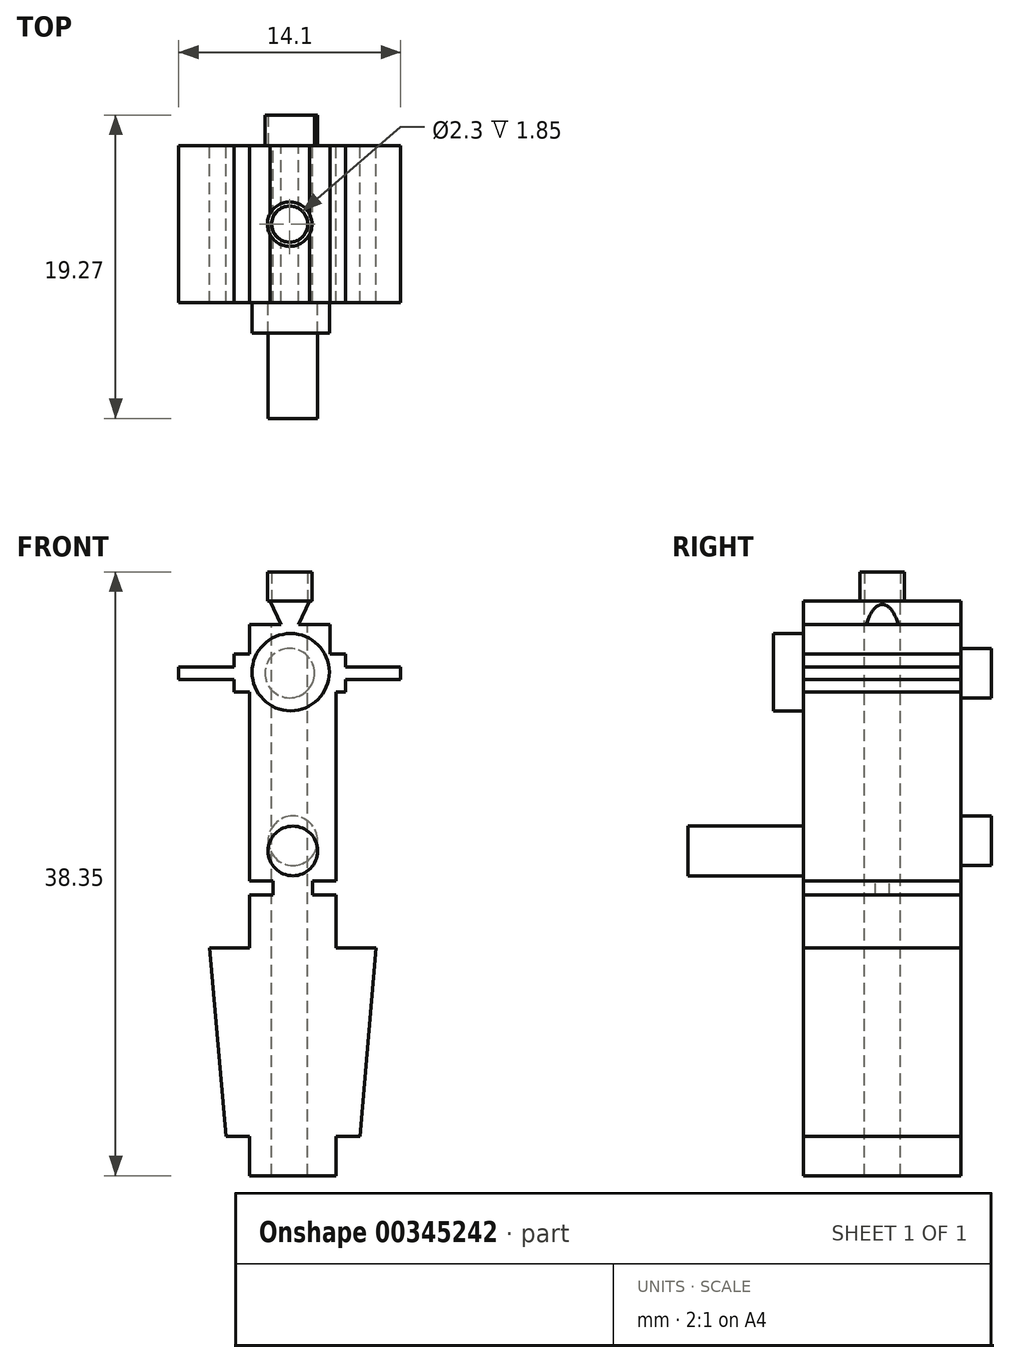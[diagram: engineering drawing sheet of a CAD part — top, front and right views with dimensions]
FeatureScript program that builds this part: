
annotation { "Feature Type Name" : "Feature", "Feature Type Description" : "" }
export const myFeature = defineFeature(function(context is Context, id is Id, definition is map)
    precondition{}
    {
        {
            var Q0;
            Q0=qCreatedBy(makeId("Front.planeOp"),FACE);
            var sketch = newSketch(context, id + "F0", { "sketchPlane" : qUnion([Q0])});
            skLineSegment(sketch, "E0", {"start": v(0, 0) * mm, "end": v(5.5, 0) * mm});
            skLineSegment(sketch, "E1", {"start": v(5.5, 0) * mm, "end": v(5.5, 2.5) * mm});
            skLineSegment(sketch, "E2", {"start": v(0, 0) * mm, "end": v(0, 2.5) * mm});
            skLineSegment(sketch, "E3", {"start": v(0, 2.5) * mm, "end": v(-1.5, 2.5) * mm});
            skLineSegment(sketch, "E4", {"start": v(5.5, 2.5) * mm, "end": v(7, 2.5) * mm});
            skLineSegment(sketch, "E5", {"start": v(7, 2.5) * mm, "end": v(8.05, 14.45) * mm});
            skLineSegment(sketch, "E6", {"start": v(-1.5, 2.5) * mm, "end": v(-2.55, 14.45) * mm});
            skLineSegment(sketch, "E7", {"start": v(8.05, 14.45) * mm, "end": v(5.5, 14.45) * mm});
            skLineSegment(sketch, "E8", {"start": v(-2.55, 14.45) * mm, "end": v(0, 14.45) * mm});
            skLineSegment(sketch, "E9", {"start": v(0, 14.45) * mm, "end": v(0, 17.82) * mm});
            skLineSegment(sketch, "E10", {"start": v(5.5, 14.45) * mm, "end": v(5.5, 17.82) * mm});
            skLineSegment(sketch, "E11", {"start": v(5.5, 17.82) * mm, "end": v(4, 17.82) * mm});
            skLineSegment(sketch, "E12", {"start": v(0, 17.82) * mm, "end": v(1.5, 17.82) * mm});
            skLineSegment(sketch, "E13", {"start": v(4, 17.82) * mm, "end": v(4, 18.72) * mm});
            skLineSegment(sketch, "E14", {"start": v(1.5, 17.82) * mm, "end": v(1.5, 18.72) * mm});
            skLineSegment(sketch, "E15", {"start": v(1.5, 18.72) * mm, "end": v(0, 18.72) * mm});
            skLineSegment(sketch, "E16", {"start": v(4, 18.72) * mm, "end": v(5.5, 18.72) * mm});
            skLineSegment(sketch, "E17", {"start": v(5.5, 18.72) * mm, "end": v(5.5, 30.72) * mm});
            skLineSegment(sketch, "E18", {"start": v(0, 18.72) * mm, "end": v(0, 30.72) * mm});
            skLineSegment(sketch, "E19", {"start": v(5.1, 33.12) * mm, "end": v(6.1, 33.12) * mm});
            skLineSegment(sketch, "E20", {"start": v(6.1, 33.12) * mm, "end": v(6.1, 32.32) * mm});
            skLineSegment(sketch, "E21", {"start": v(6.1, 32.32) * mm, "end": v(9.6, 32.32) * mm});
            skLineSegment(sketch, "E22", {"start": v(9.6, 32.32) * mm, "end": v(9.6, 31.52) * mm});
            skLineSegment(sketch, "E23", {"start": v(9.6, 31.52) * mm, "end": v(6.1, 31.52) * mm});
            skLineSegment(sketch, "E24", {"start": v(6.1, 31.52) * mm, "end": v(6.1, 30.72) * mm});
            skLineSegment(sketch, "E25", {"start": v(6.1, 30.72) * mm, "end": v(5.5, 30.72) * mm});
            skLineSegment(sketch, "E26", {"start": v(0, 30.72) * mm, "end": v(-1, 30.72) * mm});
            skLineSegment(sketch, "E27", {"start": v(-1, 30.72) * mm, "end": v(-1, 31.52) * mm});
            skLineSegment(sketch, "E28", {"start": v(-1, 31.52) * mm, "end": v(-4.5, 31.52) * mm});
            skLineSegment(sketch, "E29", {"start": v(-4.5, 31.52) * mm, "end": v(-4.5, 32.32) * mm});
            skLineSegment(sketch, "E30", {"start": v(-4.5, 32.32) * mm, "end": v(-1, 32.32) * mm});
            skLineSegment(sketch, "E31", {"start": v(-1, 32.32) * mm, "end": v(-1, 33.12) * mm});
            skLineSegment(sketch, "E32", {"start": v(-1, 33.12) * mm, "end": v(0, 33.12) * mm});
            skLineSegment(sketch, "E33", {"start": v(0, 33.12) * mm, "end": v(0, 35) * mm});
            skLineSegment(sketch, "E34", {"start": v(0, 35) * mm, "end": v(2, 35) * mm});
            skLineSegment(sketch, "E35", {"start": v(2, 35) * mm, "end": v(1.3, 36.5) * mm});
            skLineSegment(sketch, "E36", {"start": v(1.3, 36.5) * mm, "end": v(3.8, 36.5) * mm});
            skLineSegment(sketch, "E37", {"start": v(3.8, 36.5) * mm, "end": v(3.1, 35) * mm});
            skLineSegment(sketch, "E38", {"start": v(3.1, 35) * mm, "end": v(5.1, 35) * mm});
            skLineSegment(sketch, "E39", {"start": v(5.1, 35) * mm, "end": v(5.1, 33.12) * mm});
            skSolve(sketch);
        }
        {
            var Q0;
            Q0 = qSketchRegion(id + "F0", true);
            extrude(context, id + "F1", {"entities" : qUnion([Q0]), "depth" : 10 * mm});
        }
        {
            var Q0;
            Q0=makeQuery(id+"F1.opExtrude","CAP_FACE",FACE,{"disambiguationData":[OSD([sQuery(id+"F0.wireOp",EDGE,"E0"),sQuery(id+"F0.wireOp",EDGE,"E1"),sQuery(id+"F0.wireOp",EDGE,"E2"),sQuery(id+"F0.wireOp",EDGE,"E3"),sQuery(id+"F0.wireOp",EDGE,"E4"),sQuery(id+"F0.wireOp",EDGE,"E5"),sQuery(id+"F0.wireOp",EDGE,"E6"),sQuery(id+"F0.wireOp",EDGE,"E7"),sQuery(id+"F0.wireOp",EDGE,"E8"),sQuery(id+"F0.wireOp",EDGE,"E9"),sQuery(id+"F0.wireOp",EDGE,"E10"),sQuery(id+"F0.wireOp",EDGE,"E11"),sQuery(id+"F0.wireOp",EDGE,"E12"),sQuery(id+"F0.wireOp",EDGE,"E13"),sQuery(id+"F0.wireOp",EDGE,"E14"),sQuery(id+"F0.wireOp",EDGE,"E15"),sQuery(id+"F0.wireOp",EDGE,"E16"),sQuery(id+"F0.wireOp",EDGE,"E17"),sQuery(id+"F0.wireOp",EDGE,"E18"),sQuery(id+"F0.wireOp",EDGE,"E19"),sQuery(id+"F0.wireOp",EDGE,"E20"),sQuery(id+"F0.wireOp",EDGE,"E21"),sQuery(id+"F0.wireOp",EDGE,"E22"),sQuery(id+"F0.wireOp",EDGE,"E23"),sQuery(id+"F0.wireOp",EDGE,"E24"),sQuery(id+"F0.wireOp",EDGE,"E25"),sQuery(id+"F0.wireOp",EDGE,"E26"),sQuery(id+"F0.wireOp",EDGE,"E27"),sQuery(id+"F0.wireOp",EDGE,"E28"),sQuery(id+"F0.wireOp",EDGE,"E29"),sQuery(id+"F0.wireOp",EDGE,"E30"),sQuery(id+"F0.wireOp",EDGE,"E31"),sQuery(id+"F0.wireOp",EDGE,"E32"),sQuery(id+"F0.wireOp",EDGE,"E33"),sQuery(id+"F0.wireOp",EDGE,"E34"),sQuery(id+"F0.wireOp",EDGE,"E35"),sQuery(id+"F0.wireOp",EDGE,"E36"),sQuery(id+"F0.wireOp",EDGE,"E37"),sQuery(id+"F0.wireOp",EDGE,"E38"),sQuery(id+"F0.wireOp",EDGE,"E39")])],"isStart":false});
            var sketch = newSketch(context, id + "F2", { "sketchPlane" : qUnion([Q0])});
            skCircle(sketch, "E40", {"center": v(2.6, 31.98) * mm, "radius": 2.45 * mm});
            skCircle(sketch, "E41", {"center": v(2.75, 20.63) * mm, "radius": 1.57 * mm});
            skPoint(sketch, "E41.centerSnap0", {"position": v(2.75, 0) * mm});
            skSolve(sketch);
        }
        {
            var Q0;
            Q0=makeQuery(id+"F2.imprint","IMPRINT",FACE,{"disambiguationData":[TD([[makeQuery(id+"F2.imprint","IMPRINT",EDGE,{"derivedFrom":sQuery(id+"F2.wireOp",EDGE,"E40")}),1.0]])]});
            var Q1;
            Q1=makeQuery(id+"F2.imprint","IMPRINT",FACE,{"disambiguationData":[TD([[makeQuery(id+"F2.imprint","IMPRINT",EDGE,{"derivedFrom":sQuery(id+"F2.wireOp",EDGE,"E41")}),1.0]])]});
            extrude(context, id + "F3", {"entities" : qUnion([Q0, Q1]), "operationType" : NewBodyOperationType.ADD, "depth" : 1.93 * mm});
        }
        {
            var Q0;
            Q0=makeQuery(id+"F3.opExtrude","CAP_FACE",FACE,{"disambiguationData":[OSD([sQuery(id+"F2.wireOp",EDGE,"E41")])],"isStart":false});
            extrude(context, id + "F4", {"entities" : qUnion([Q0]), "operationType" : NewBodyOperationType.ADD, "depth" : 5.4 * mm});
        }
        {
            var Q0;
            Q0=makeQuery(id+"F1.opExtrude","SWEPT_FACE",FACE,{"disambiguationData":[OSD([sQuery(id+"F0.wireOp",EDGE,"E36")])]});
            var sketch = newSketch(context, id + "F5", { "sketchPlane" : qUnion([Q0])});
            skCircle(sketch, "E42", {"center": v(2.55, -5) * mm, "radius": 1.14 * mm});
            skPoint(sketch, "E42.centerSnap0", {"position": v(2.55, 0) * mm});
            skPoint(sketch, "E42.centerSnap1", {"position": v(1.3, -5) * mm});
            skSolve(sketch);
        }
        {
            var Q0;
            Q0 = qSketchRegion(id + "F5", true);
            extrude(context, id + "F6", {"entities" : qUnion([Q0]), "operationType" : NewBodyOperationType.REMOVE, "oppositeDirection" : true, "depth" : 90 * mm});
        }
        {
            var Q0;
            Q0=makeQuery(id+"F1.opExtrude","SWEPT_FACE",FACE,{"disambiguationData":[OSD([sQuery(id+"F0.wireOp",EDGE,"E36")])]});
            var sketch = newSketch(context, id + "F7", { "sketchPlane" : qUnion([Q0])});
            skCircle(sketch, "E43", {"center": v(2.55, -5) * mm, "radius": 1.42 * mm});
            skSolve(sketch);
        }
        {
            var Q0;
            Q0 = qSketchRegion(id + "F7", true);
            extrude(context, id + "F8", {"entities" : qUnion([Q0]), "operationType" : NewBodyOperationType.ADD, "depth" : 1.85 * mm});
        }
        {
            var Q0;
            Q0=makeQuery(id+"F8.boolean.opBoolean","SPLIT",FACE,{"disambiguationData":[TD([makeQuery(id+"F6.boolean.opBoolean","COPY",FACE,{"derivedFrom":makeQuery(id+"F6.opExtrude","SWEPT_FACE",FACE,{"disambiguationData":[OSD([sQuery(id+"F5.wireOp",EDGE,"E42")])]})})])],"derivedFrom":makeQuery(id+"F8.opExtrude","CAP_FACE",FACE,{"disambiguationData":[OSD([sQuery(id+"F7.wireOp",EDGE,"E43")])],"isStart":true})});
            var sketch = newSketch(context, id + "F9", { "sketchPlane" : qUnion([Q0])});
            skCircle(sketch, "E44", {"center": v(2.55, 5) * mm, "radius": 1.15 * mm});
            skSolve(sketch);
        }
        {
            var Q0;
            Q0 = qSketchRegion(id + "F9", true);
            extrude(context, id + "F10", {"entities" : qUnion([Q0]), "operationType" : NewBodyOperationType.REMOVE, "oppositeDirection" : true, "depth" : 90 * mm});
        }
        {
            var Q0;
            Q0=makeQuery(id+"F1.opExtrude","CAP_FACE",FACE,{"disambiguationData":[OSD([sQuery(id+"F0.wireOp",EDGE,"E0"),sQuery(id+"F0.wireOp",EDGE,"E1"),sQuery(id+"F0.wireOp",EDGE,"E2"),sQuery(id+"F0.wireOp",EDGE,"E3"),sQuery(id+"F0.wireOp",EDGE,"E4"),sQuery(id+"F0.wireOp",EDGE,"E5"),sQuery(id+"F0.wireOp",EDGE,"E6"),sQuery(id+"F0.wireOp",EDGE,"E7"),sQuery(id+"F0.wireOp",EDGE,"E8"),sQuery(id+"F0.wireOp",EDGE,"E9"),sQuery(id+"F0.wireOp",EDGE,"E10"),sQuery(id+"F0.wireOp",EDGE,"E11"),sQuery(id+"F0.wireOp",EDGE,"E12"),sQuery(id+"F0.wireOp",EDGE,"E13"),sQuery(id+"F0.wireOp",EDGE,"E14"),sQuery(id+"F0.wireOp",EDGE,"E15"),sQuery(id+"F0.wireOp",EDGE,"E16"),sQuery(id+"F0.wireOp",EDGE,"E17"),sQuery(id+"F0.wireOp",EDGE,"E18"),sQuery(id+"F0.wireOp",EDGE,"E19"),sQuery(id+"F0.wireOp",EDGE,"E20"),sQuery(id+"F0.wireOp",EDGE,"E21"),sQuery(id+"F0.wireOp",EDGE,"E22"),sQuery(id+"F0.wireOp",EDGE,"E23"),sQuery(id+"F0.wireOp",EDGE,"E24"),sQuery(id+"F0.wireOp",EDGE,"E25"),sQuery(id+"F0.wireOp",EDGE,"E26"),sQuery(id+"F0.wireOp",EDGE,"E27"),sQuery(id+"F0.wireOp",EDGE,"E28"),sQuery(id+"F0.wireOp",EDGE,"E29"),sQuery(id+"F0.wireOp",EDGE,"E30"),sQuery(id+"F0.wireOp",EDGE,"E31"),sQuery(id+"F0.wireOp",EDGE,"E32"),sQuery(id+"F0.wireOp",EDGE,"E33"),sQuery(id+"F0.wireOp",EDGE,"E34"),sQuery(id+"F0.wireOp",EDGE,"E35"),sQuery(id+"F0.wireOp",EDGE,"E36"),sQuery(id+"F0.wireOp",EDGE,"E37"),sQuery(id+"F0.wireOp",EDGE,"E38"),sQuery(id+"F0.wireOp",EDGE,"E39")])],"isStart":true});
            var sketch = newSketch(context, id + "F11", { "sketchPlane" : qUnion([Q0])});
            skPoint(sketch, "E45.centerSnap0", {"position": v(-2.55, 36.5) * mm});
            skPoint(sketch, "E45.centerSnap1", {"position": v(4.5, 31.92) * mm});
            skCircle(sketch, "E46", {"center": v(-2.55, 31.92) * mm, "radius": 1.57 * mm});
            skSolve(sketch);
        }
        {
            var Q0;
            Q0 = qSketchRegion(id + "F11", true);
            extrude(context, id + "F12", {"entities" : qUnion([Q0]), "operationType" : NewBodyOperationType.ADD, "depth" : 1.93 * mm});
        }
        {
            var Q0;
            Q0=makeQuery(id+"F1.opExtrude","CAP_FACE",FACE,{"disambiguationData":[OSD([sQuery(id+"F0.wireOp",EDGE,"E0"),sQuery(id+"F0.wireOp",EDGE,"E1"),sQuery(id+"F0.wireOp",EDGE,"E2"),sQuery(id+"F0.wireOp",EDGE,"E3"),sQuery(id+"F0.wireOp",EDGE,"E4"),sQuery(id+"F0.wireOp",EDGE,"E5"),sQuery(id+"F0.wireOp",EDGE,"E6"),sQuery(id+"F0.wireOp",EDGE,"E7"),sQuery(id+"F0.wireOp",EDGE,"E8"),sQuery(id+"F0.wireOp",EDGE,"E9"),sQuery(id+"F0.wireOp",EDGE,"E10"),sQuery(id+"F0.wireOp",EDGE,"E11"),sQuery(id+"F0.wireOp",EDGE,"E12"),sQuery(id+"F0.wireOp",EDGE,"E13"),sQuery(id+"F0.wireOp",EDGE,"E14"),sQuery(id+"F0.wireOp",EDGE,"E15"),sQuery(id+"F0.wireOp",EDGE,"E16"),sQuery(id+"F0.wireOp",EDGE,"E17"),sQuery(id+"F0.wireOp",EDGE,"E18"),sQuery(id+"F0.wireOp",EDGE,"E19"),sQuery(id+"F0.wireOp",EDGE,"E20"),sQuery(id+"F0.wireOp",EDGE,"E21"),sQuery(id+"F0.wireOp",EDGE,"E22"),sQuery(id+"F0.wireOp",EDGE,"E23"),sQuery(id+"F0.wireOp",EDGE,"E24"),sQuery(id+"F0.wireOp",EDGE,"E25"),sQuery(id+"F0.wireOp",EDGE,"E26"),sQuery(id+"F0.wireOp",EDGE,"E27"),sQuery(id+"F0.wireOp",EDGE,"E28"),sQuery(id+"F0.wireOp",EDGE,"E29"),sQuery(id+"F0.wireOp",EDGE,"E30"),sQuery(id+"F0.wireOp",EDGE,"E31"),sQuery(id+"F0.wireOp",EDGE,"E32"),sQuery(id+"F0.wireOp",EDGE,"E33"),sQuery(id+"F0.wireOp",EDGE,"E34"),sQuery(id+"F0.wireOp",EDGE,"E35"),sQuery(id+"F0.wireOp",EDGE,"E36"),sQuery(id+"F0.wireOp",EDGE,"E37"),sQuery(id+"F0.wireOp",EDGE,"E38"),sQuery(id+"F0.wireOp",EDGE,"E39")])],"isStart":true});
            var sketch = newSketch(context, id + "F13", { "sketchPlane" : qUnion([Q0])});
            skCircle(sketch, "E47", {"center": v(-2.75, 21.27) * mm, "radius": 1.57 * mm});
            skPoint(sketch, "E47.centerSnap0", {"position": v(-2.75, 0) * mm});
            skSolve(sketch);
        }
        {
            var Q0;
            Q0 = qSketchRegion(id + "F13", true);
            extrude(context, id + "F14", {"entities" : qUnion([Q0]), "operationType" : NewBodyOperationType.ADD, "depth" : 1.93 * mm});
        }
    });
